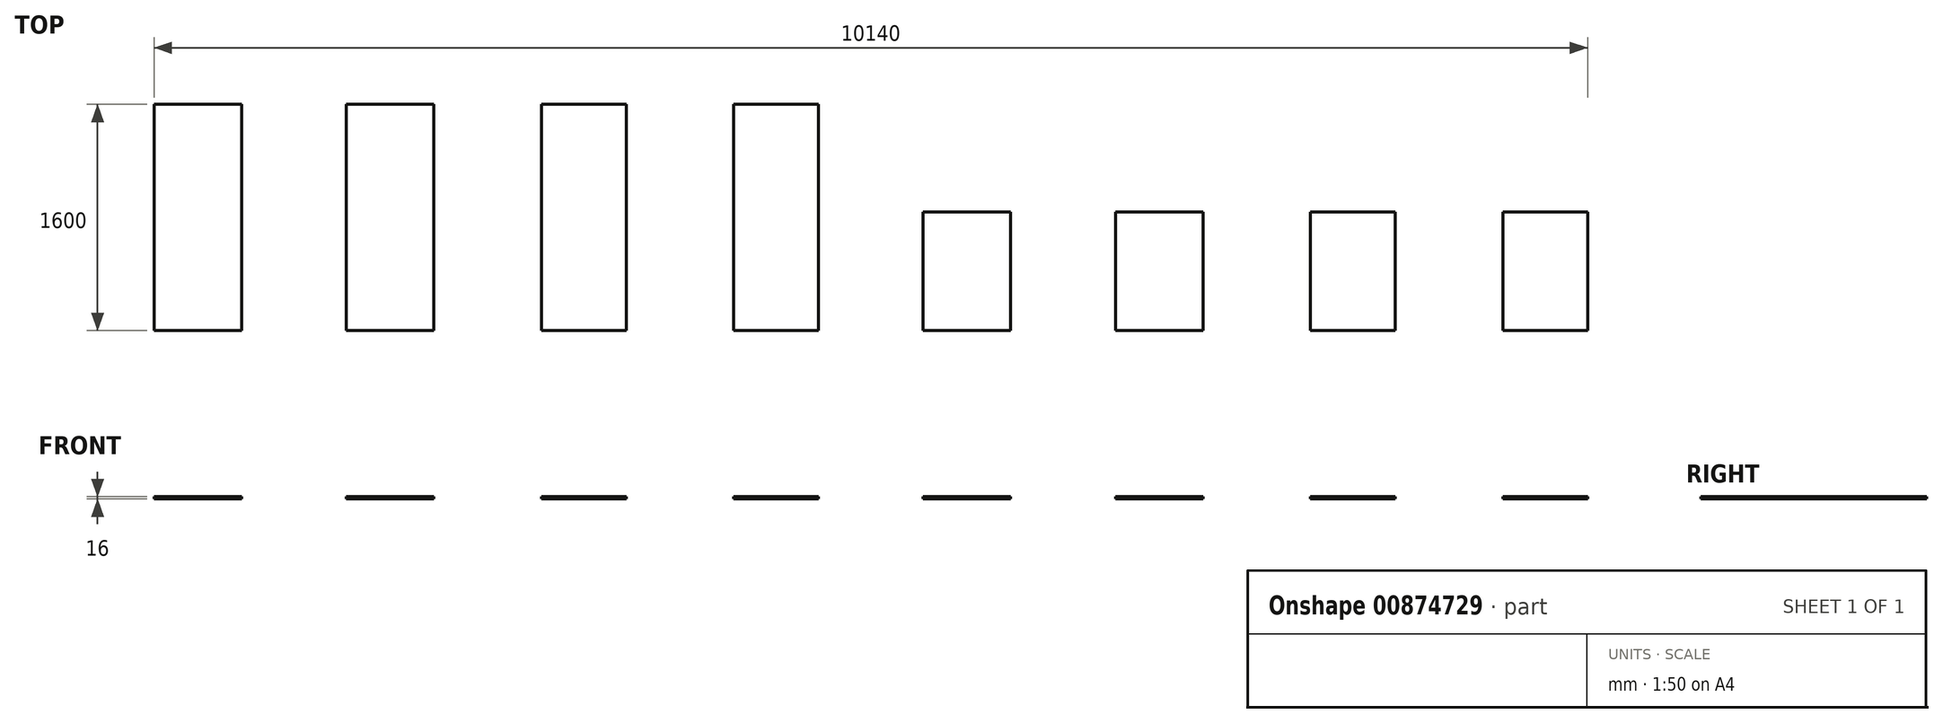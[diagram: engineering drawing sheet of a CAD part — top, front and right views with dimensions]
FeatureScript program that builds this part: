
annotation { "Feature Type Name" : "Feature", "Feature Type Description" : "" }
export const myFeature = defineFeature(function(context is Context, id is Id, definition is map)
    precondition{}
    {
        {
            var Q0;
            Q0=qCreatedBy(makeId("Top.planeOp"),FACE);
            var sketch = newSketch(context, id + "F0", { "sketchPlane" : qUnion([Q0])});
            skLineSegment(sketch, "E0.bottom", {"start": v(0, 0) * mm, "end": v(1000, 0) * mm, "construction": true});
            skLineSegment(sketch, "E0.top", {"start": v(0, 2000) * mm, "end": v(1000, 2000) * mm, "construction": true});
            skLineSegment(sketch, "E0.left", {"start": v(0, 0) * mm, "end": v(0, 2000) * mm, "construction": true});
            skLineSegment(sketch, "E0.right", {"start": v(1000, 0) * mm, "end": v(1000, 2000) * mm, "construction": true});
            skLineSegment(sketch, "E1.0", {"start": v(20, 20) * mm, "end": v(20, 1980) * mm, "construction": true});
            skLineSegment(sketch, "E1.1", {"start": v(20, 20) * mm, "end": v(980, 20) * mm, "construction": true});
            skLineSegment(sketch, "E1.2", {"start": v(980, 20) * mm, "end": v(980, 1980) * mm, "construction": true});
            skLineSegment(sketch, "E1.3", {"start": v(20, 1980) * mm, "end": v(980, 1980) * mm, "construction": true});
            skLineSegment(sketch, "E2.1.0.0", {"start": v(1360, 0) * mm, "end": v(1360, 2000) * mm, "construction": true});
            skLineSegment(sketch, "E2.1.0.1", {"start": v(1380, 20) * mm, "end": v(2340, 20) * mm, "construction": true});
            skLineSegment(sketch, "E2.1.0.2", {"start": v(1380, 1980) * mm, "end": v(2340, 1980) * mm, "construction": true});
            skLineSegment(sketch, "E2.1.0.3", {"start": v(2340, 20) * mm, "end": v(2340, 1980) * mm, "construction": true});
            skLineSegment(sketch, "E2.1.0.4", {"start": v(1360, 0) * mm, "end": v(2360, 0) * mm, "construction": true});
            skLineSegment(sketch, "E2.1.0.5", {"start": v(1380, 20) * mm, "end": v(1380, 1980) * mm, "construction": true});
            skLineSegment(sketch, "E2.1.0.6", {"start": v(1360, 2000) * mm, "end": v(2360, 2000) * mm, "construction": true});
            skLineSegment(sketch, "E2.1.0.7", {"start": v(2360, 0) * mm, "end": v(2360, 2000) * mm, "construction": true});
            skLineSegment(sketch, "E2.2.0.0", {"start": v(2720, 0) * mm, "end": v(2720, 2000) * mm, "construction": true});
            skLineSegment(sketch, "E2.2.0.1", {"start": v(2740, 20) * mm, "end": v(3700, 20) * mm, "construction": true});
            skLineSegment(sketch, "E2.2.0.2", {"start": v(2740, 1980) * mm, "end": v(3700, 1980) * mm, "construction": true});
            skLineSegment(sketch, "E2.2.0.3", {"start": v(3700, 20) * mm, "end": v(3700, 1980) * mm, "construction": true});
            skLineSegment(sketch, "E2.2.0.4", {"start": v(2720, 0) * mm, "end": v(3720, 0) * mm, "construction": true});
            skLineSegment(sketch, "E2.2.0.5", {"start": v(2740, 20) * mm, "end": v(2740, 1980) * mm, "construction": true});
            skLineSegment(sketch, "E2.2.0.6", {"start": v(2720, 2000) * mm, "end": v(3720, 2000) * mm, "construction": true});
            skLineSegment(sketch, "E2.2.0.7", {"start": v(3720, 0) * mm, "end": v(3720, 2000) * mm, "construction": true});
            skLineSegment(sketch, "E2.3.0.0", {"start": v(4080, 0) * mm, "end": v(4080, 2000) * mm, "construction": true});
            skLineSegment(sketch, "E2.3.0.1", {"start": v(4100, 20) * mm, "end": v(5060, 20) * mm, "construction": true});
            skLineSegment(sketch, "E2.3.0.2", {"start": v(4100, 1980) * mm, "end": v(5060, 1980) * mm, "construction": true});
            skLineSegment(sketch, "E2.3.0.3", {"start": v(5060, 20) * mm, "end": v(5060, 1980) * mm, "construction": true});
            skLineSegment(sketch, "E2.3.0.4", {"start": v(4080, 0) * mm, "end": v(5080, 0) * mm, "construction": true});
            skLineSegment(sketch, "E2.3.0.5", {"start": v(4100, 20) * mm, "end": v(4100, 1980) * mm, "construction": true});
            skLineSegment(sketch, "E2.3.0.6", {"start": v(4080, 2000) * mm, "end": v(5080, 2000) * mm, "construction": true});
            skLineSegment(sketch, "E2.3.0.7", {"start": v(5080, 0) * mm, "end": v(5080, 2000) * mm, "construction": true});
            skLineSegment(sketch, "E2.4.0.0", {"start": v(5440, 0) * mm, "end": v(5440, 2000) * mm, "construction": true});
            skLineSegment(sketch, "E2.4.0.1", {"start": v(5460, 20) * mm, "end": v(6420, 20) * mm, "construction": true});
            skLineSegment(sketch, "E2.4.0.2", {"start": v(5460, 1980) * mm, "end": v(6420, 1980) * mm, "construction": true});
            skLineSegment(sketch, "E2.4.0.3", {"start": v(6420, 20) * mm, "end": v(6420, 1980) * mm, "construction": true});
            skLineSegment(sketch, "E2.4.0.4", {"start": v(5440, 0) * mm, "end": v(6440, 0) * mm, "construction": true});
            skLineSegment(sketch, "E2.4.0.5", {"start": v(5460, 20) * mm, "end": v(5460, 1980) * mm, "construction": true});
            skLineSegment(sketch, "E2.4.0.6", {"start": v(5440, 2000) * mm, "end": v(6440, 2000) * mm, "construction": true});
            skLineSegment(sketch, "E2.4.0.7", {"start": v(6440, 0) * mm, "end": v(6440, 2000) * mm, "construction": true});
            skLineSegment(sketch, "E2.direction1", {"start": v(1000, 0) * mm, "end": v(2360, 0) * mm, "construction": true});
            skLineSegment(sketch, "E3.0.5.0", {"start": v(6800, 0) * mm, "end": v(6800, 2000) * mm, "construction": true});
            skLineSegment(sketch, "E3.3.5.0", {"start": v(6820, 20) * mm, "end": v(7780, 20) * mm, "construction": true});
            skLineSegment(sketch, "E3.6.5.0", {"start": v(6820, 1980) * mm, "end": v(7780, 1980) * mm, "construction": true});
            skLineSegment(sketch, "E3.9.5.0", {"start": v(7780, 20) * mm, "end": v(7780, 1980) * mm, "construction": true});
            skLineSegment(sketch, "E3.12.5.0", {"start": v(6800, 0) * mm, "end": v(7800, 0) * mm, "construction": true});
            skLineSegment(sketch, "E3.15.5.0", {"start": v(6820, 20) * mm, "end": v(6820, 1980) * mm, "construction": true});
            skLineSegment(sketch, "E3.18.5.0", {"start": v(6800, 2000) * mm, "end": v(7800, 2000) * mm, "construction": true});
            skLineSegment(sketch, "E3.21.5.0", {"start": v(7800, 0) * mm, "end": v(7800, 2000) * mm, "construction": true});
            skLineSegment(sketch, "E3.0.6.0", {"start": v(8160, 0) * mm, "end": v(8160, 2000) * mm, "construction": true});
            skLineSegment(sketch, "E3.3.6.0", {"start": v(8180, 20) * mm, "end": v(9140, 20) * mm, "construction": true});
            skLineSegment(sketch, "E3.6.6.0", {"start": v(8180, 1980) * mm, "end": v(9140, 1980) * mm, "construction": true});
            skLineSegment(sketch, "E3.9.6.0", {"start": v(9140, 20) * mm, "end": v(9140, 1980) * mm, "construction": true});
            skLineSegment(sketch, "E3.12.6.0", {"start": v(8160, 0) * mm, "end": v(9160, 0) * mm, "construction": true});
            skLineSegment(sketch, "E3.15.6.0", {"start": v(8180, 20) * mm, "end": v(8180, 1980) * mm, "construction": true});
            skLineSegment(sketch, "E3.18.6.0", {"start": v(8160, 2000) * mm, "end": v(9160, 2000) * mm, "construction": true});
            skLineSegment(sketch, "E3.21.6.0", {"start": v(9160, 0) * mm, "end": v(9160, 2000) * mm, "construction": true});
            skLineSegment(sketch, "E3.0.7.0", {"start": v(9520, 0) * mm, "end": v(9520, 2000) * mm, "construction": true});
            skLineSegment(sketch, "E3.3.7.0", {"start": v(9540, 20) * mm, "end": v(10500, 20) * mm, "construction": true});
            skLineSegment(sketch, "E3.6.7.0", {"start": v(9540, 1980) * mm, "end": v(10500, 1980) * mm, "construction": true});
            skLineSegment(sketch, "E3.9.7.0", {"start": v(10500, 20) * mm, "end": v(10500, 1980) * mm, "construction": true});
            skLineSegment(sketch, "E3.12.7.0", {"start": v(9520, 0) * mm, "end": v(10520, 0) * mm, "construction": true});
            skLineSegment(sketch, "E3.15.7.0", {"start": v(9540, 20) * mm, "end": v(9540, 1980) * mm, "construction": true});
            skLineSegment(sketch, "E3.18.7.0", {"start": v(9520, 2000) * mm, "end": v(10520, 2000) * mm, "construction": true});
            skLineSegment(sketch, "E3.21.7.0", {"start": v(10520, 0) * mm, "end": v(10520, 2000) * mm, "construction": true});
            skSolve(sketch);
        }
        {
            var Q0;
            Q0=qCreatedBy(makeId("Top.planeOp"),FACE);
            var sketch = newSketch(context, id + "F1", { "sketchPlane" : qUnion([Q0])});
            skLineSegment(sketch, "E4.bottom", {"start": v(980, 20) * mm, "end": v(360, 20) * mm});
            skLineSegment(sketch, "E4.top", {"start": v(980, 1620) * mm, "end": v(360, 1620) * mm});
            skLineSegment(sketch, "E4.left", {"start": v(980, 20) * mm, "end": v(980, 1620) * mm});
            skLineSegment(sketch, "E4.right", {"start": v(360, 20) * mm, "end": v(360, 1620) * mm});
            skPoint(sketch, "E5", {"position": v(2340, 20) * mm});
            skPoint(sketch, "E6", {"position": v(3700, 20) * mm});
            skPoint(sketch, "E7", {"position": v(5060, 20) * mm});
            skPoint(sketch, "E8", {"position": v(6420, 20) * mm});
            skPoint(sketch, "E9", {"position": v(10500, 20) * mm});
            skPoint(sketch, "E10", {"position": v(9140, 20) * mm});
            skPoint(sketch, "E11", {"position": v(7780, 20) * mm});
            skLineSegment(sketch, "E12.bottom", {"start": v(2340, 20) * mm, "end": v(1720, 20) * mm});
            skLineSegment(sketch, "E12.top", {"start": v(2340, 1620) * mm, "end": v(1720, 1620) * mm});
            skLineSegment(sketch, "E12.left", {"start": v(2340, 20) * mm, "end": v(2340, 1620) * mm});
            skLineSegment(sketch, "E12.right", {"start": v(1720, 20) * mm, "end": v(1720, 1620) * mm});
            skLineSegment(sketch, "E13.bottom", {"start": v(3700, 20) * mm, "end": v(3100, 20) * mm});
            skLineSegment(sketch, "E13.top", {"start": v(3700, 1620) * mm, "end": v(3100, 1620) * mm});
            skLineSegment(sketch, "E13.left", {"start": v(3700, 20) * mm, "end": v(3700, 1620) * mm});
            skLineSegment(sketch, "E13.right", {"start": v(3100, 20) * mm, "end": v(3100, 1620) * mm});
            skLineSegment(sketch, "E14.bottom", {"start": v(5060, 20) * mm, "end": v(4460, 20) * mm});
            skLineSegment(sketch, "E14.top", {"start": v(5060, 1620) * mm, "end": v(4460, 1620) * mm});
            skLineSegment(sketch, "E14.left", {"start": v(5060, 20) * mm, "end": v(5060, 1620) * mm});
            skLineSegment(sketch, "E14.right", {"start": v(4460, 20) * mm, "end": v(4460, 1620) * mm});
            skLineSegment(sketch, "E15.bottom", {"start": v(6420, 20) * mm, "end": v(5800, 20) * mm});
            skLineSegment(sketch, "E15.top", {"start": v(6420, 860) * mm, "end": v(5800, 860) * mm});
            skLineSegment(sketch, "E15.left", {"start": v(6420, 20) * mm, "end": v(6420, 860) * mm});
            skLineSegment(sketch, "E15.right", {"start": v(5800, 20) * mm, "end": v(5800, 860) * mm});
            skLineSegment(sketch, "E16.bottom", {"start": v(7780, 20) * mm, "end": v(7160, 20) * mm});
            skLineSegment(sketch, "E16.top", {"start": v(7780, 860) * mm, "end": v(7160, 860) * mm});
            skLineSegment(sketch, "E16.left", {"start": v(7780, 20) * mm, "end": v(7780, 860) * mm});
            skLineSegment(sketch, "E16.right", {"start": v(7160, 20) * mm, "end": v(7160, 860) * mm});
            skLineSegment(sketch, "E17.bottom", {"start": v(9140, 20) * mm, "end": v(8540, 20) * mm});
            skLineSegment(sketch, "E17.top", {"start": v(9140, 860) * mm, "end": v(8540, 860) * mm});
            skLineSegment(sketch, "E17.left", {"start": v(9140, 20) * mm, "end": v(9140, 860) * mm});
            skLineSegment(sketch, "E17.right", {"start": v(8540, 20) * mm, "end": v(8540, 860) * mm});
            skLineSegment(sketch, "E18.bottom", {"start": v(10500, 20) * mm, "end": v(9900, 20) * mm});
            skLineSegment(sketch, "E18.top", {"start": v(10500, 860) * mm, "end": v(9900, 860) * mm});
            skLineSegment(sketch, "E18.left", {"start": v(10500, 20) * mm, "end": v(10500, 860) * mm});
            skLineSegment(sketch, "E18.right", {"start": v(9900, 20) * mm, "end": v(9900, 860) * mm});
            skSolve(sketch);
        }
        {
            var Q0;
            Q0 = qSketchRegion(id + "F1", true);
            extrude(context, id + "F2", {"entities" : qUnion([Q0]), "depth" : 16 * mm, "offsetDistance" : 25 * mm});
        }
    });
